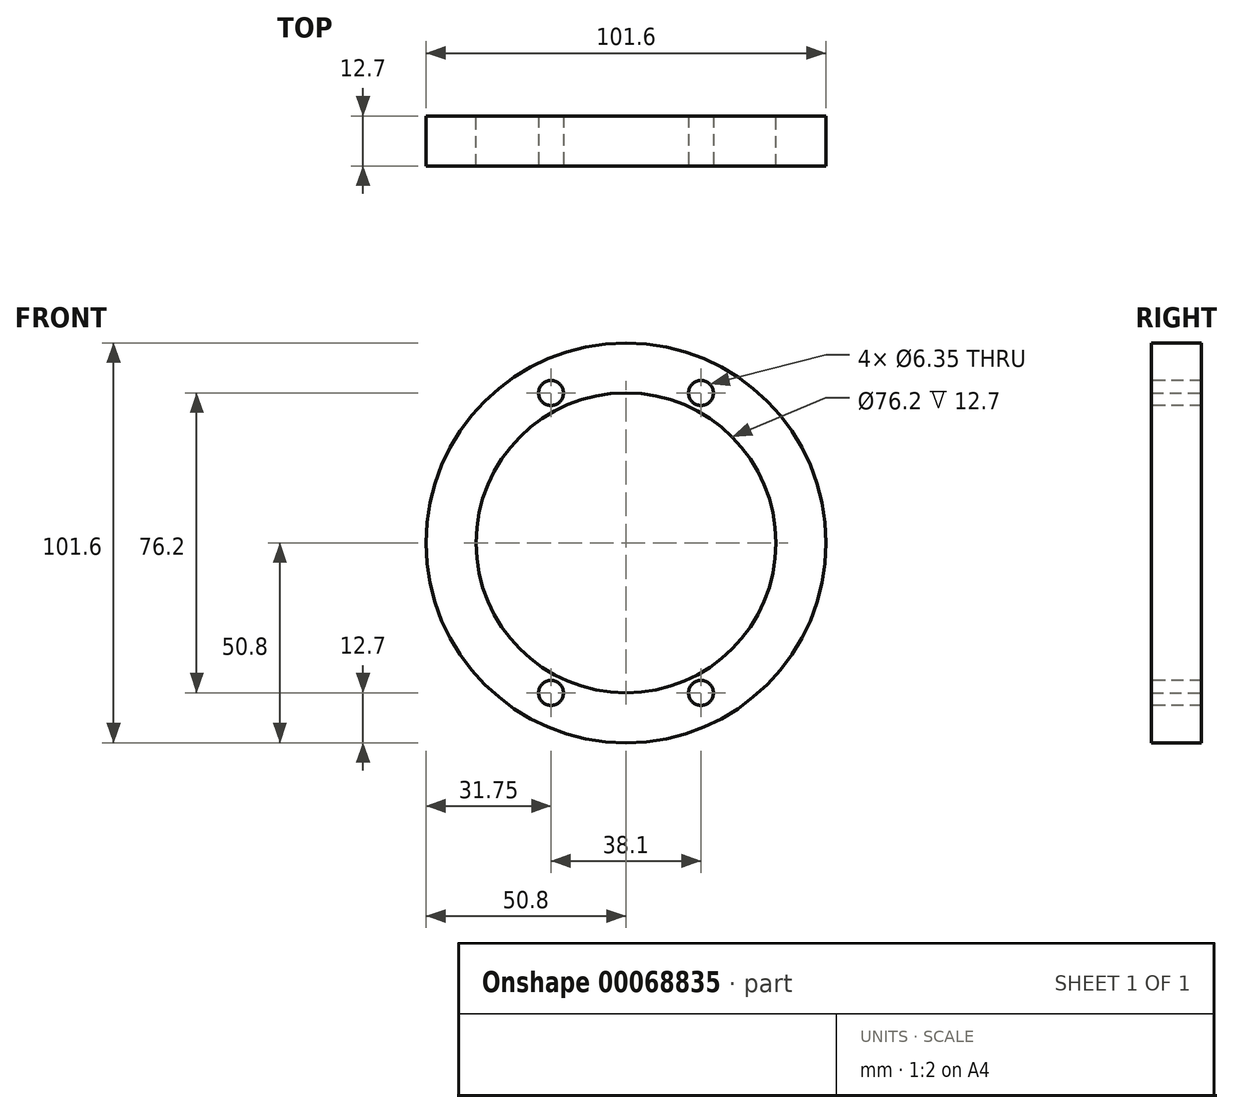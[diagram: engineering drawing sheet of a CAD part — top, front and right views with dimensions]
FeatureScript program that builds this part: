
annotation { "Feature Type Name" : "Feature", "Feature Type Description" : "" }
export const myFeature = defineFeature(function(context is Context, id is Id, definition is map)
    precondition{}
    {
        {
            var Q0;
            Q0=qCreatedBy(makeId("Front.planeOp"),FACE);
            var sketch = newSketch(context, id + "F0", { "sketchPlane" : qUnion([Q0])});
            skCircle(sketch, "E0", {"center": v(0, 0) * mm, "radius": 50.8 * mm});
            skCircle(sketch, "E1", {"center": v(0, 0) * mm, "radius": 38.1 * mm});
            skCircle(sketch, "E2", {"center": v(0, 0) * mm, "radius": 34.93 * mm, "construction": true});
            skPoint(sketch, "E3", {"position": v(0, 34.93) * mm});
            skPoint(sketch, "E4", {"position": v(-34.93, 0) * mm});
            skPoint(sketch, "E5", {"position": v(0, -34.92) * mm});
            skPoint(sketch, "E6", {"position": v(34.93, 0) * mm});
            skSolve(sketch);
        }
        {
            var Q0;
            Q0=qSketchRegion(id+"F0",true);
            extrude(context, id + "F1", {"entities" : qUnion([Q0]), "depth" : 12.7 * mm});
        }
        {
            var Q0;
            Q0=makeQuery(id+"F1.opExtrude","CAP_FACE",FACE,{"disambiguationData":[OSD([sQuery(id+"F0.wireOp",EDGE,"E0"),sQuery(id+"F0.wireOp",EDGE,"E1")])],"isStart":false});
            var sketch = newSketch(context, id + "F2", { "sketchPlane" : qUnion([Q0])});
            skCircle(sketch, "E7", {"center": v(-19.05, 38.1) * mm, "radius": 3.18 * mm});
            skCircle(sketch, "E8", {"center": v(19.05, 38.1) * mm, "radius": 3.18 * mm});
            skCircle(sketch, "E9", {"center": v(19.05, -38.1) * mm, "radius": 3.18 * mm});
            skCircle(sketch, "E10", {"center": v(-19.05, -38.1) * mm, "radius": 3.18 * mm});
            skLineSegment(sketch, "E11.bottom", {"start": v(-19.05, -38.1) * mm, "end": v(19.05, -38.1) * mm, "construction": true});
            skLineSegment(sketch, "E11.top", {"start": v(-19.05, 38.1) * mm, "end": v(19.05, 38.1) * mm, "construction": true});
            skLineSegment(sketch, "E11.left", {"start": v(-19.05, -38.1) * mm, "end": v(-19.05, 38.1) * mm, "construction": true});
            skLineSegment(sketch, "E11.right", {"start": v(19.05, -38.1) * mm, "end": v(19.05, 38.1) * mm, "construction": true});
            skSolve(sketch);
        }
        {
            var Q0;
            Q0 = qSketchRegion(id + "F2", true);
            extrude(context, id + "F3", {"entities" : qUnion([Q0]), "operationType" : NewBodyOperationType.REMOVE, "oppositeDirection" : true, "depth" : 12.7 * mm});
        }
    });
